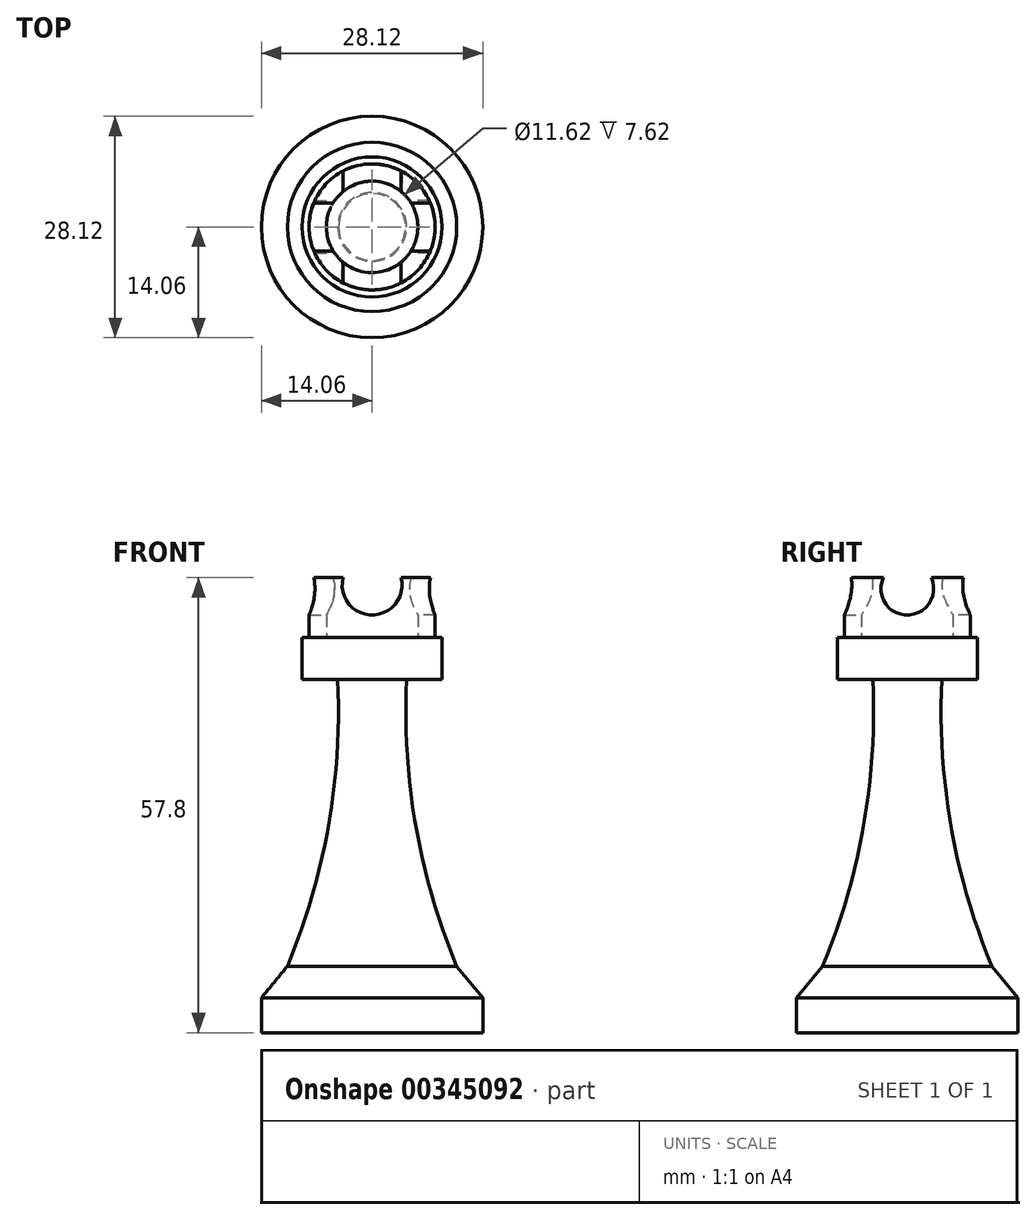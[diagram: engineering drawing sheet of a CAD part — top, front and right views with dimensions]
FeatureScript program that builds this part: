
annotation { "Feature Type Name" : "Feature", "Feature Type Description" : "" }
export const myFeature = defineFeature(function(context is Context, id is Id, definition is map)
    precondition{}
    {
        {
            var Q0;
            Q0=qCreatedBy(makeId("Front.planeOp"),FACE);
            var sketch = newSketch(context, id + "F0", { "sketchPlane" : qUnion([Q0])});
            skLineSegment(sketch, "E0", {"start": v(0, 0) * mm, "end": v(0, 44.45) * mm});
            skPoint(sketch, "E1.end.orphan", {"position": v(0, 38.76) * mm});
            skPoint(sketch, "E2.end.orphan", {"position": v(15, 0) * mm});
            skLineSegment(sketch, "E3", {"start": v(0, 0) * mm, "end": v(10.75, 0) * mm});
            skArc(sketch, "E4", {"start": v(4.37, 36.4) * mm, "mid": v(5.55, 17.85) * mm, "end": v(10.75, 0) * mm});
            skPoint(sketch, "E5.start.orphan", {"position": v(7.2, 38.76) * mm});
            skLineSegment(sketch, "E6", {"start": v(4.37, 36.4) * mm, "end": v(0, 36.4) * mm});
            skSolve(sketch);
        }
        {
            var Q0;
            Q0 = qSketchRegion(id + "F0", true);
            var Q1;
            Q1=sQuery(id+"F0.wireOp",EDGE,"E0");
            revolve(context, id + "F1", {"entities" : qUnion([Q0]), "axis" : qUnion([Q1]), "revolveType" : RevolveType.FULL});
        }
        {
            var Q0;
            Q0=qCreatedBy(makeId("Front.planeOp"),FACE);
            var sketch = newSketch(context, id + "F2", { "sketchPlane" : qUnion([Q0])});
            skLineSegment(sketch, "E7", {"start": v(0, 0) * mm, "end": v(10.75, 0) * mm});
            skLineSegment(sketch, "E8", {"start": v(10.75, 0) * mm, "end": v(14.06, -4.02) * mm});
            skLineSegment(sketch, "E9", {"start": v(14.06, -4.02) * mm, "end": v(0, -4.02) * mm});
            skLineSegment(sketch, "E10", {"start": v(0, -4.02) * mm, "end": v(0, 0) * mm});
            skLineSegment(sketch, "E11", {"start": v(14.06, -4.02) * mm, "end": v(14.06, -5.9) * mm});
            skLineSegment(sketch, "E12", {"start": v(14.06, -5.9) * mm, "end": v(0, -5.9) * mm});
            skLineSegment(sketch, "E13", {"start": v(0, -5.9) * mm, "end": v(0, -4.02) * mm});
            skLineSegment(sketch, "E14", {"start": v(14.06, -5.9) * mm, "end": v(14.06, -8.45) * mm});
            skLineSegment(sketch, "E15", {"start": v(14.06, -8.45) * mm, "end": v(0, -8.45) * mm});
            skLineSegment(sketch, "E16", {"start": v(0, -8.45) * mm, "end": v(0, -5.9) * mm});
            skSolve(sketch);
        }
        {
            var Q0;
            Q0 = qSketchRegion(id + "F2", true);
            var Q1;
            Q1=sQuery(id+"F2.wireOp",EDGE,"E13");
            revolve(context, id + "F3", {"operationType" : NewBodyOperationType.ADD, "entities" : qUnion([Q0]), "axis" : qUnion([Q1]), "revolveType" : RevolveType.FULL});
        }
        {
            var Q0;
            Q0=makeQuery(id+"F1.opRevolve","SWEPT_FACE",FACE,{"disambiguationData":[OSD([sQuery(id+"F0.wireOp",EDGE,"E6")])]});
            var sketch = newSketch(context, id + "F4", { "sketchPlane" : qUnion([Q0])});
            skPoint(sketch, "E17.center.orphan", {"position": v(0, 0) * mm});
            skCircle(sketch, "E18", {"center": v(0, 0) * mm, "radius": 8.9 * mm});
            skSolve(sketch);
        }
        {
            var Q0;
            Q0 = qSketchRegion(id + "F4", true);
            extrude(context, id + "F5", {"entities" : qUnion([Q0]), "operationType" : NewBodyOperationType.ADD, "depth" : 5.33 * mm, "offsetDistance" : 25.4 * mm});
        }
        {
            var Q0;
            Q0=makeQuery(id+"F5.opExtrude","CAP_FACE",FACE,{"disambiguationData":[OSD([sQuery(id+"F4.wireOp",EDGE,"E18")])],"isStart":false});
            var sketch = newSketch(context, id + "F6", { "sketchPlane" : qUnion([Q0])});
            skCircle(sketch, "E19", {"center": v(0, 0) * mm, "radius": 8 * mm});
            skCircle(sketch, "E20", {"center": v(0, 0) * mm, "radius": 5.8 * mm});
            skSolve(sketch);
        }
        {
            var Q0;
            Q0 = qSketchRegion(id + "F6", true);
            extrude(context, id + "F7", {"entities" : qUnion([Q0]), "operationType" : NewBodyOperationType.ADD, "depth" : 7.62 * mm, "offsetDistance" : 25.4 * mm});
        }
        {
            var Q0;
            Q0=qCreatedBy(makeId("Front.planeOp"),FACE);
            var sketch = newSketch(context, id + "F8", { "sketchPlane" : qUnion([Q0])});
            skCircle(sketch, "E21", {"center": v(0, 48.4) * mm, "radius": 3.8 * mm});
            skSolve(sketch);
        }
        {
            var Q0;
            Q0 = qSketchRegion(id + "F8", true);
            extrude(context, id + "F9", {"entities" : qUnion([Q0]), "operationType" : NewBodyOperationType.REMOVE, "oppositeDirection" : true, "depth" : 25.4 * mm, "offsetDistance" : 25.4 * mm});
        }
        {
            var Q0;
            Q0 = qSketchRegion(id + "F8", true);
            extrude(context, id + "F10", {"entities" : qUnion([Q0]), "operationType" : NewBodyOperationType.REMOVE, "depth" : 98.55 * mm, "offsetDistance" : 25.4 * mm});
        }
        {
            var Q0;
            Q0=qCreatedBy(makeId("Right.planeOp"),FACE);
            var sketch = newSketch(context, id + "F11", { "sketchPlane" : qUnion([Q0])});
            skCircle(sketch, "E22", {"center": v(0, 47.96) * mm, "radius": 3.35 * mm});
            skSolve(sketch);
        }
        {
            var Q0;
            Q0 = qSketchRegion(id + "F11", true);
            extrude(context, id + "F12", {"entities" : qUnion([Q0]), "operationType" : NewBodyOperationType.REMOVE, "oppositeDirection" : true, "depth" : 25.4 * mm, "offsetDistance" : 25.4 * mm});
        }
        {
            var Q0;
            Q0 = qSketchRegion(id + "F11", true);
            extrude(context, id + "F13", {"entities" : qUnion([Q0]), "operationType" : NewBodyOperationType.REMOVE, "depth" : 156.97 * mm, "offsetDistance" : 25.4 * mm});
        }
    });
